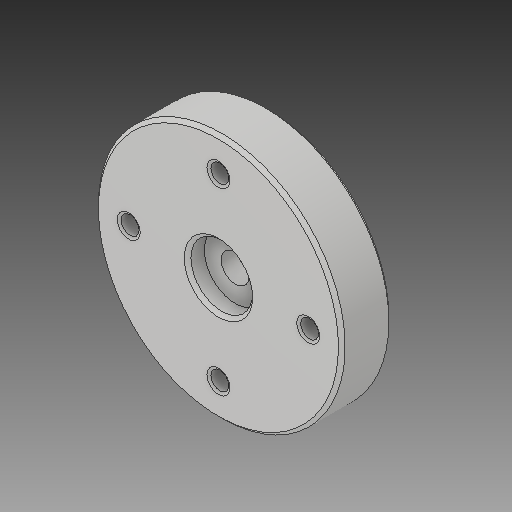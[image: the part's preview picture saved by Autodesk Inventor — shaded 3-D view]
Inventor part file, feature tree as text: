
AUTODESK INVENTOR PART (.ipt)
format: ipt  version: 2018 (Build 220112000, 112)  size: 145,920 bytes
history: native  units: mm
features: other x1, chamfer x1
ambient origin geometry x8: Origin, YZ Plane, XZ Plane, XY Plane, X Axis, Y Axis, Z Axis, Center Point
bodies: Body1 (feature_tree)
feature tree (2):
  other  "Твердое тело1"
  chamfer  "Chamfer1"  [1 undecoded]
note: 1 required parameter value undecoded (feature->parameter linkage not recoverable at this tier; creation-order binding heuristic only, values carry confidence <= 0.55)
